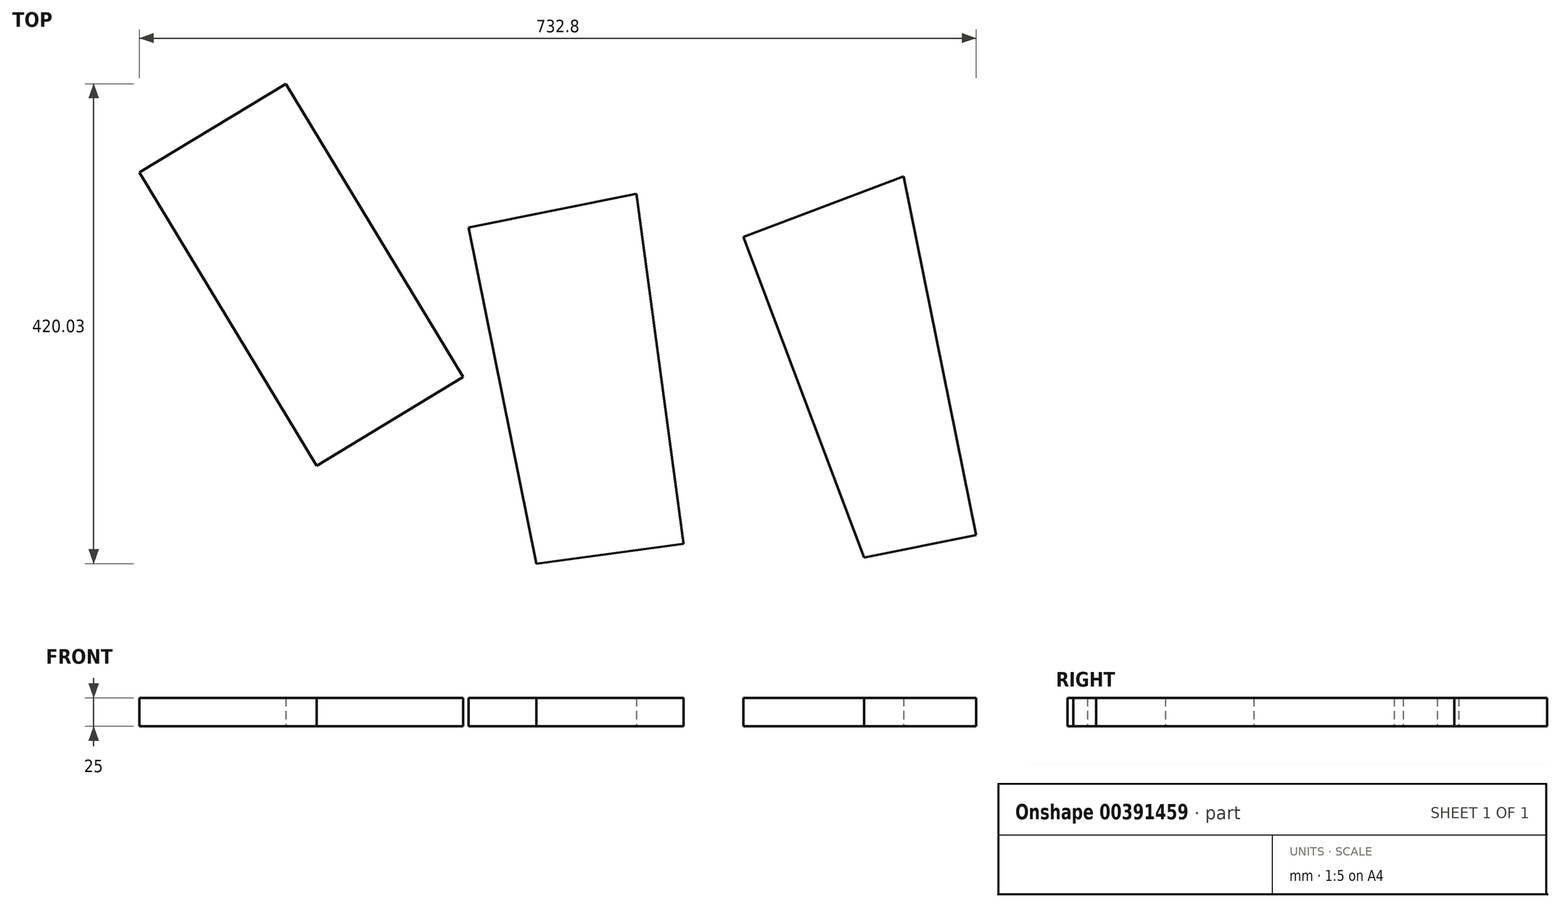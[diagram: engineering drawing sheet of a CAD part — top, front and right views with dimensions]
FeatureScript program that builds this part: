
annotation { "Feature Type Name" : "Feature", "Feature Type Description" : "" }
export const myFeature = defineFeature(function(context is Context, id is Id, definition is map)
    precondition{}
    {
        {
            var Q0;
            Q0=qCreatedBy(makeId("Top.planeOp"),FACE);
            var sketch = newSketch(context, id + "F0", { "sketchPlane" : qUnion([Q0])});
            skLineSegment(sketch, "E0", {"start": v(516.25, 1244.12) * mm, "end": v(639.24, 1273.15) * mm});
            skLineSegment(sketch, "E1", {"start": v(639.24, 1273.15) * mm, "end": v(691.65, 1051.06) * mm});
            skLineSegment(sketch, "E2", {"start": v(691.65, 1051.06) * mm, "end": v(568.66, 1022.03) * mm});
            skLineSegment(sketch, "E3", {"start": v(568.66, 1022.03) * mm, "end": v(516.25, 1244.12) * mm});
            skLineSegment(sketch, "E4", {"start": v(691.65, 1051.06) * mm, "end": v(758.1, 1058.97) * mm});
            skLineSegment(sketch, "E5", {"start": v(758.1, 1058.97) * mm, "end": v(756.88, 1287.16) * mm});
            skLineSegment(sketch, "E6", {"start": v(756.88, 1287.16) * mm, "end": v(639.24, 1273.15) * mm});
            skLineSegment(sketch, "E7", {"start": v(756.88, 1287.16) * mm, "end": v(758.1, 1058.97) * mm});
            skLineSegment(sketch, "E8", {"start": v(758.1, 1058.97) * mm, "end": v(829.25, 1051.17) * mm});
            skLineSegment(sketch, "E9", {"start": v(829.25, 1051.17) * mm, "end": v(879.84, 1273.69) * mm});
            skLineSegment(sketch, "E10", {"start": v(879.84, 1273.69) * mm, "end": v(756.88, 1287.16) * mm});
            skLineSegment(sketch, "E11", {"start": v(879.84, 1273.69) * mm, "end": v(829.25, 1051.17) * mm});
            skLineSegment(sketch, "E12", {"start": v(829.25, 1051.17) * mm, "end": v(910.73, 1026.63) * mm});
            skLineSegment(sketch, "E13", {"start": v(910.73, 1026.63) * mm, "end": v(991.44, 1240.07) * mm});
            skLineSegment(sketch, "E14", {"start": v(991.44, 1240.07) * mm, "end": v(879.84, 1273.69) * mm});
            skLineSegment(sketch, "E15", {"start": v(577.74, 1258.64) * mm, "end": v(630.16, 1036.54) * mm});
            skLineSegment(sketch, "E16", {"start": v(698.06, 1280.15) * mm, "end": v(724.87, 1055.01) * mm});
            skLineSegment(sketch, "E17", {"start": v(818.36, 1280.42) * mm, "end": v(793.67, 1055.07) * mm});
            skLineSegment(sketch, "E18", {"start": v(935.64, 1256.88) * mm, "end": v(869.99, 1038.9) * mm});
            skLineSegment(sketch, "E19", {"start": v(516.25, 1244.12) * mm, "end": v(758.1, 1058.97) * mm});
            skLineSegment(sketch, "E20", {"start": v(639.24, 1273.15) * mm, "end": v(829.25, 1051.17) * mm});
            skLineSegment(sketch, "E21", {"start": v(756.88, 1287.16) * mm, "end": v(910.73, 1026.63) * mm});
            skLineSegment(sketch, "E22", {"start": v(639.24, 1273.15) * mm, "end": v(563.27, 1208.12) * mm});
            skLineSegment(sketch, "E23", {"start": v(758.1, 1058.97) * mm, "end": v(788.53, 1098.73) * mm});
            skLineSegment(sketch, "E24", {"start": v(829.25, 1051.17) * mm, "end": v(873.74, 1089.26) * mm});
            skLineSegment(sketch, "E25", {"start": v(756.88, 1287.16) * mm, "end": v(670.77, 1236.31) * mm});
            skLineSegment(sketch, "E26", {"start": v(758.1, 1058.97) * mm, "end": v(795.3, 1090.82) * mm, "construction": true});
            skLineSegment(sketch, "E27", {"start": v(829.25, 1051.17) * mm, "end": v(878.91, 1080.5) * mm, "construction": true});
            skLineSegment(sketch, "E28", {"start": v(991.44, 1240.07) * mm, "end": v(1088.94, 1200.25) * mm});
            skLineSegment(sketch, "E29", {"start": v(1088.94, 1200.25) * mm, "end": v(997.15, 991.33) * mm});
            skLineSegment(sketch, "E30", {"start": v(910.73, 1026.63) * mm, "end": v(997.15, 991.33) * mm});
            skLineSegment(sketch, "E31", {"start": v(953.94, 1008.98) * mm, "end": v(1040.2, 1220.16) * mm});
            skLineSegment(sketch, "E32", {"start": v(879.84, 1273.69) * mm, "end": v(997.15, 991.33) * mm});
            skLineSegment(sketch, "E33", {"start": v(879.84, 1273.69) * mm, "end": v(787.5, 1235.32) * mm});
            skLineSegment(sketch, "E34", {"start": v(910.73, 1026.63) * mm, "end": v(968.35, 1060.66) * mm});
            skLineSegment(sketch, "E35", {"start": v(910.73, 1026.63) * mm, "end": v(971.92, 1052.06) * mm});
            skSolve(sketch);
        }
        {
            var Q0;
            Q0=qCreatedBy(makeId("Top.planeOp"),FACE);
            var sketch = newSketch(context, id + "F1", { "sketchPlane" : qUnion([Q0])});
            skLineSegment(sketch, "E36", {"start": v(135.48, 1698.96) * mm, "end": v(263.87, 1776.53) * mm});
            skLineSegment(sketch, "E37", {"start": v(263.87, 1776.53) * mm, "end": v(419, 1519.75) * mm});
            skLineSegment(sketch, "E38", {"start": v(419, 1519.75) * mm, "end": v(290.62, 1442.19) * mm});
            skLineSegment(sketch, "E39", {"start": v(290.62, 1442.19) * mm, "end": v(135.48, 1698.96) * mm});
            skLineSegment(sketch, "E40", {"start": v(423.7, 1650.56) * mm, "end": v(483.13, 1356.5) * mm});
            skLineSegment(sketch, "E41", {"start": v(483.13, 1356.5) * mm, "end": v(611.97, 1373.85) * mm});
            skLineSegment(sketch, "E42", {"start": v(611.97, 1373.85) * mm, "end": v(570.72, 1680.27) * mm});
            skLineSegment(sketch, "E43", {"start": v(570.72, 1680.27) * mm, "end": v(423.7, 1650.56) * mm});
            skLineSegment(sketch, "E44", {"start": v(664.48, 1642.46) * mm, "end": v(770.26, 1361.73) * mm});
            skLineSegment(sketch, "E45", {"start": v(770.26, 1361.73) * mm, "end": v(868.28, 1381.54) * mm});
            skLineSegment(sketch, "E46", {"start": v(868.28, 1381.54) * mm, "end": v(804.85, 1695.35) * mm});
            skLineSegment(sketch, "E47", {"start": v(804.85, 1695.35) * mm, "end": v(664.48, 1642.46) * mm});
            skSolve(sketch);
        }
        {
            var Q0;
            Q0=makeQuery(id+"F1.imprint","IMPRINT",FACE,{"disambiguationData":[TD([[makeQuery(id+"F1.imprint","IMPRINT",EDGE,{"derivedFrom":sQuery(id+"F1.wireOp",EDGE,"E36")}),-1.0]])]});
            var Q1;
            Q1=makeQuery(id+"F1.imprint","IMPRINT",FACE,{"disambiguationData":[TD([[makeQuery(id+"F1.imprint","IMPRINT",EDGE,{"derivedFrom":sQuery(id+"F1.wireOp",EDGE,"E40")}),1.0]])]});
            var Q2;
            Q2=makeQuery(id+"F1.imprint","IMPRINT",FACE,{"disambiguationData":[TD([[makeQuery(id+"F1.imprint","IMPRINT",EDGE,{"derivedFrom":sQuery(id+"F1.wireOp",EDGE,"E44")}),1.0]])]});
            extrude(context, id + "F2", {"entities" : qUnion([Q0, Q1, Q2]), "depth" : 25 * mm});
        }
    });
